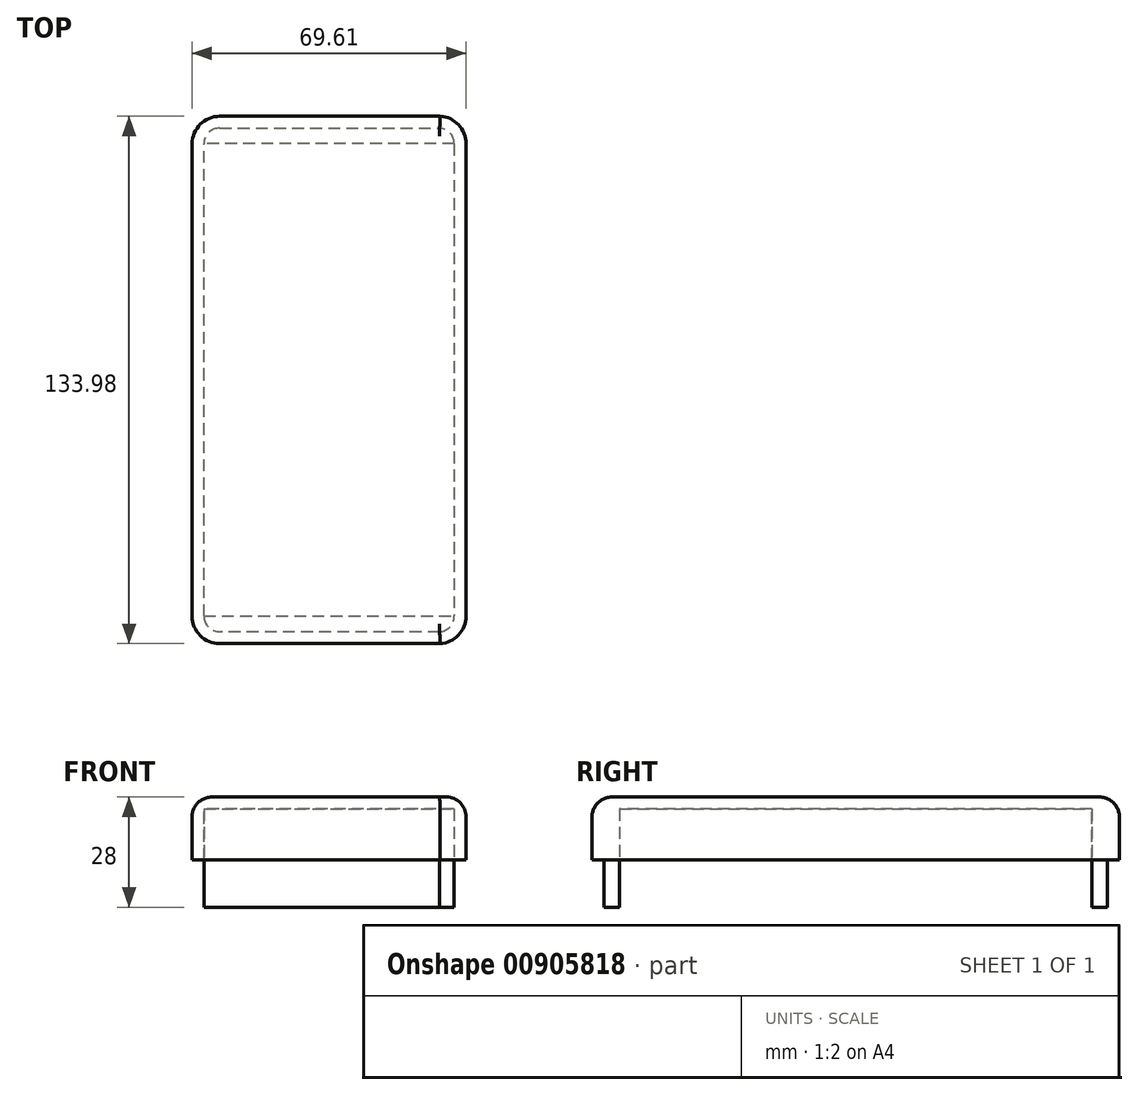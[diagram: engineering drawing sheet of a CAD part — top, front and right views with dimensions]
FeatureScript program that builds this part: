
annotation { "Feature Type Name" : "Feature", "Feature Type Description" : "" }
export const myFeature = defineFeature(function(context is Context, id is Id, definition is map)
    precondition{}
    {
        {
            var Q0;
            Q0=qCreatedBy(makeId("Top.planeOp"),FACE);
            var sketch = newSketch(context, id + "F0", { "sketchPlane" : qUnion([Q0])});
            skLineSegment(sketch, "E0", {"start": v(34.6, 0) * mm, "end": v(34.6, -60) * mm});
            skLineSegment(sketch, "E1", {"start": v(-35.02, -59.99) * mm, "end": v(-35, -0.01) * mm});
            skLineSegment(sketch, "E2", {"start": v(-0.02, -66.99) * mm, "end": v(27.98, -66.99) * mm});
            skLineSegment(sketch, "E3", {"start": v(-0.02, -66.99) * mm, "end": v(-28.02, -66.99) * mm});
            skArc(sketch, "E4", {"start": v(-35.02, -59.99) * mm, "mid": v(-32.97, -64.94) * mm, "end": v(-28.02, -66.99) * mm});
            skArc(sketch, "E5", {"start": v(27.98, -66.99) * mm, "mid": v(32.68, -64.81) * mm, "end": v(34.6, -60) * mm});
            skLineSegment(sketch, "E6", {"start": v(34.6, 0) * mm, "end": v(34.6, 60) * mm});
            skLineSegment(sketch, "E7", {"start": v(-35, -0.01) * mm, "end": v(-35, 59.99) * mm});
            skLineSegment(sketch, "E8", {"start": v(-28, 66.99) * mm, "end": v(28, 66.99) * mm});
            skArc(sketch, "E9", {"start": v(-28, 66.99) * mm, "mid": v(-32.95, 64.94) * mm, "end": v(-35, 59.99) * mm});
            skArc(sketch, "E10", {"start": v(34.6, 60) * mm, "mid": v(32.68, 64.8) * mm, "end": v(28, 66.99) * mm});
            skSolve(sketch);
        }
        {
            var Q0;
            Q0=qSketchRegion(id+"F0",true);
            extrude(context, id + "F1", {"entities" : qUnion([Q0]), "depth" : 16 * mm, "offsetDistance" : 25 * mm});
        }
        {
            var Q0;
            Q0=makeQuery(id+"F1.opExtrude","CAP_FACE",FACE,{"disambiguationData":[OSD([sQuery(id+"F0.wireOp",EDGE,"E0"),sQuery(id+"F0.wireOp",EDGE,"E1"),sQuery(id+"F0.wireOp",EDGE,"E2"),sQuery(id+"F0.wireOp",EDGE,"E3"),sQuery(id+"F0.wireOp",EDGE,"E4"),sQuery(id+"F0.wireOp",EDGE,"E5"),sQuery(id+"F0.wireOp",EDGE,"E6"),sQuery(id+"F0.wireOp",EDGE,"E7"),sQuery(id+"F0.wireOp",EDGE,"E8"),sQuery(id+"F0.wireOp",EDGE,"E9"),sQuery(id+"F0.wireOp",EDGE,"E10")])],"isStart":true});
            shell(context, id + "F2", {"entities" : qUnion([Q0]), "thickness" : 3 * mm});
        }
        {
            var Q0;
            Q0=makeQuery(id+"F1.opExtrude","CAP_FACE",FACE,{"disambiguationData":[OSD([sQuery(id+"F0.wireOp",EDGE,"E0"),sQuery(id+"F0.wireOp",EDGE,"E1"),sQuery(id+"F0.wireOp",EDGE,"E2"),sQuery(id+"F0.wireOp",EDGE,"E3"),sQuery(id+"F0.wireOp",EDGE,"E4"),sQuery(id+"F0.wireOp",EDGE,"E5"),sQuery(id+"F0.wireOp",EDGE,"E6"),sQuery(id+"F0.wireOp",EDGE,"E7"),sQuery(id+"F0.wireOp",EDGE,"E8"),sQuery(id+"F0.wireOp",EDGE,"E9"),sQuery(id+"F0.wireOp",EDGE,"E10")])],"isStart":false});
            fillet(context, id + "F3", {"entities" : qUnion([Q0]), "radius" : 5 * mm, "tangentPropagation" : true, "allowEdgeOverflow" : false});
        }
        {
            var Q0;
            Q0=makeQuery(id+"F2.opShell","OFFSET_FACE",FACE,{"disambiguationData":[OSD([sQuery(id+"F0.wireOp",EDGE,"E0"),sQuery(id+"F0.wireOp",EDGE,"E1"),sQuery(id+"F0.wireOp",EDGE,"E2"),sQuery(id+"F0.wireOp",EDGE,"E3"),sQuery(id+"F0.wireOp",EDGE,"E4"),sQuery(id+"F0.wireOp",EDGE,"E5"),sQuery(id+"F0.wireOp",EDGE,"E6"),sQuery(id+"F0.wireOp",EDGE,"E7"),sQuery(id+"F0.wireOp",EDGE,"E8"),sQuery(id+"F0.wireOp",EDGE,"E9"),sQuery(id+"F0.wireOp",EDGE,"E10")])]});
            var sketch = newSketch(context, id + "F4", { "sketchPlane" : qUnion([Q0])});
            skArc(sketch, "E11.0.1", {"start": v(-32, -59.99) * mm, "mid": v(-30.83, -62.82) * mm, "end": v(-28, -63.99) * mm});
            skLineSegment(sketch, "E11.0.2", {"start": v(-28, -63.99) * mm, "end": v(27.9, -63.99) * mm});
            skArc(sketch, "E11.0.3", {"start": v(27.9, -63.99) * mm, "mid": v(30.53, -62.72) * mm, "end": v(31.6, -60) * mm});
            skArc(sketch, "E11.0.5", {"start": v(31.6, 60) * mm, "mid": v(30.52, 62.72) * mm, "end": v(27.88, 63.99) * mm});
            skLineSegment(sketch, "E11.0.6", {"start": v(27.88, 63.99) * mm, "end": v(-28.02, 63.99) * mm});
            skArc(sketch, "E11.0.7", {"start": v(-28.02, 63.99) * mm, "mid": v(-30.85, 62.82) * mm, "end": v(-32.02, 59.99) * mm});
            skLineSegment(sketch, "E12", {"start": v(-32.02, 59.99) * mm, "end": v(31.6, 60) * mm});
            skLineSegment(sketch, "E13", {"start": v(31.6, -60) * mm, "end": v(-32, -59.99) * mm});
            skSolve(sketch);
        }
        {
            var Q0;
            Q0 = qSketchRegion(id + "F4", true);
            extrude(context, id + "F5", {"entities" : qUnion([Q0]), "operationType" : NewBodyOperationType.ADD, "depth" : 25 * mm, "offsetDistance" : 25 * mm});
        }
    });
